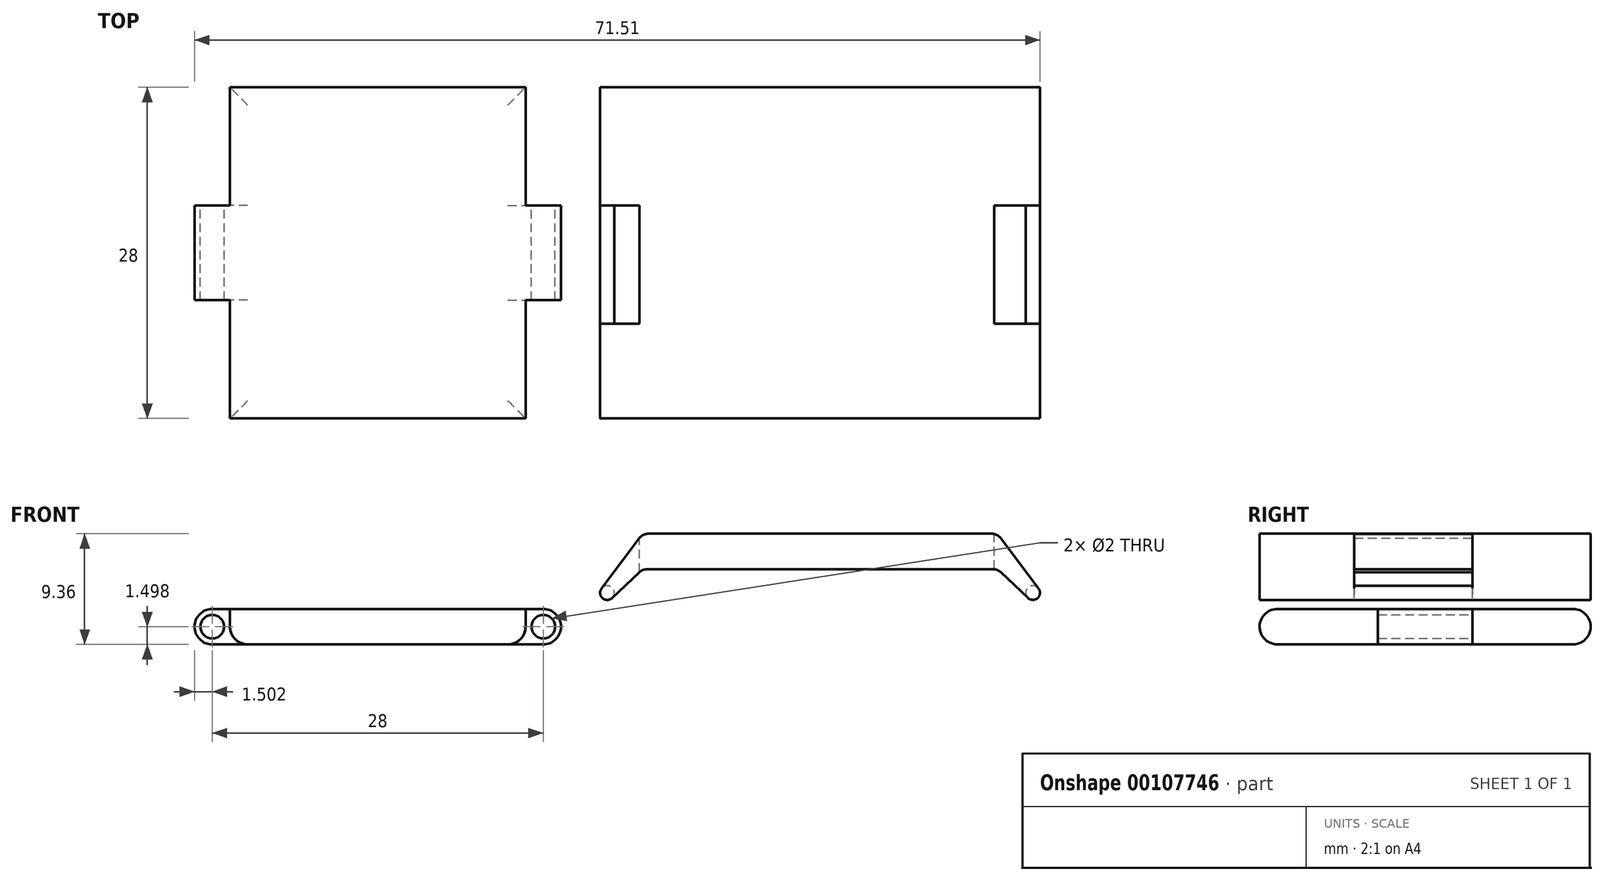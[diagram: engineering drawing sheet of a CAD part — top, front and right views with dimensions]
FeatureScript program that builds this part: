
annotation { "Feature Type Name" : "Feature", "Feature Type Description" : "" }
export const myFeature = defineFeature(function(context is Context, id is Id, definition is map)
    precondition{}
    {
        {
            var Q0;
            Q0=qCreatedBy(makeId("Front.planeOp"),FACE);
            var sketch = newSketch(context, id + "F0", { "sketchPlane" : qUnion([Q0])});
            skLineSegment(sketch, "E0.bottom", {"start": v(-39.04, 3) * mm, "end": v(-11.04, 3) * mm});
            skLineSegment(sketch, "E0.top", {"start": v(-39.04, 0) * mm, "end": v(-11.04, 0) * mm});
            skLineSegment(sketch, "E0.left", {"start": v(-39.04, 3) * mm, "end": v(-39.04, 2.5) * mm});
            skLineSegment(sketch, "E0.right", {"start": v(-11.04, 3) * mm, "end": v(-11.04, 2.5) * mm});
            skArc(sketch, "E1", {"start": v(-11.04, 0) * mm, "mid": v(-9.54, 1.5) * mm, "end": v(-11.04, 3) * mm});
            skArc(sketch, "E2", {"start": v(-39.04, 3) * mm, "mid": v(-40.54, 1.5) * mm, "end": v(-39.04, 0) * mm});
            skCircle(sketch, "E3", {"center": v(-39.04, 1.5) * mm, "radius": 1 * mm});
            skCircle(sketch, "E4", {"center": v(-11.04, 1.5) * mm, "radius": 1 * mm});
            skLineSegment(sketch, "E5.trimOffspring", {"start": v(-11.04, 0.5) * mm, "end": v(-11.04, 0) * mm});
            skLineSegment(sketch, "E6.trimOffspring", {"start": v(-39.04, 0.5) * mm, "end": v(-39.04, 0) * mm});
            skLineSegment(sketch, "E7.bottom", {"start": v(-2.27, 6.37) * mm, "end": v(26.94, 6.37) * mm});
            skLineSegment(sketch, "E7.top", {"start": v(-2.16, 9.37) * mm, "end": v(26.84, 9.37) * mm});
            skLineSegment(sketch, "E7.left", {"start": v(-2.66, 6.37) * mm, "end": v(-2.66, 9.37) * mm});
            skLineSegment(sketch, "E7.right", {"start": v(27.34, 6.37) * mm, "end": v(27.34, 9.37) * mm});
            skCircle(sketch, "E8", {"center": v(30.34, 4.37) * mm, "radius": 0.6 * mm});
            skCircle(sketch, "E9", {"center": v(-5.66, 4.37) * mm, "radius": 0.6 * mm});
            skLineSegment(sketch, "E10", {"start": v(-2.96, 8.97) * mm, "end": v(-6.14, 4.73) * mm});
            skLineSegment(sketch, "E11", {"start": v(-2.95, 6.1) * mm, "end": v(-5.25, 3.93) * mm});
            skLineSegment(sketch, "E12", {"start": v(27.64, 8.97) * mm, "end": v(30.82, 4.73) * mm});
            skLineSegment(sketch, "E13", {"start": v(27.62, 6.1) * mm, "end": v(29.92, 3.94) * mm});
            skPoint(sketch, "E14.visualSharp", {"position": v(-2.66, 9.37) * mm});
            skArc(sketch, "E14.filletArc", {"start": v(-2.16, 9.37) * mm, "mid": v(-2.61, 9.27) * mm, "end": v(-2.96, 8.97) * mm});
            skPoint(sketch, "E15.visualSharp", {"position": v(-2.66, 6.37) * mm});
            skArc(sketch, "E15.filletArc", {"start": v(-2.27, 6.37) * mm, "mid": v(-2.64, 6.3) * mm, "end": v(-2.95, 6.1) * mm});
            skPoint(sketch, "E16.visualSharp", {"position": v(27.34, 9.37) * mm});
            skArc(sketch, "E16.filletArc", {"start": v(27.64, 8.97) * mm, "mid": v(27.28, 9.27) * mm, "end": v(26.84, 9.37) * mm});
            skPoint(sketch, "E17.visualSharp", {"position": v(27.34, 6.37) * mm});
            skArc(sketch, "E17.filletArc", {"start": v(27.62, 6.1) * mm, "mid": v(27.3, 6.3) * mm, "end": v(26.94, 6.37) * mm});
            skSolve(sketch);
        }
        {
            var Q0;
            Q0=makeQuery(id+"F0.imprint","IMPRINT",FACE,{"disambiguationData":[TD([[makeQuery(id+"F0.imprint","IMPRINT",EDGE,{"derivedFrom":sQuery(id+"F0.wireOp",EDGE,"E0.bottom")}),-1.0]])]});
            var sketch = newSketch(context, id + "F1", { "sketchPlane" : qUnion([Q0])});
            skLineSegment(sketch, "E18.bottom", {"start": v(-39.07, 3) * mm, "end": v(-11.07, 3) * mm});
            skLineSegment(sketch, "E18.top", {"start": v(-39.07, 0) * mm, "end": v(-11.07, 0) * mm});
            skLineSegment(sketch, "E18.left", {"start": v(-39.07, 3) * mm, "end": v(-39.07, 2.5) * mm});
            skLineSegment(sketch, "E18.right", {"start": v(-11.07, 3) * mm, "end": v(-11.07, 2.5) * mm});
            skArc(sketch, "E19", {"start": v(-11.07, 0) * mm, "mid": v(-9.57, 1.5) * mm, "end": v(-11.07, 3) * mm});
            skArc(sketch, "E20", {"start": v(-39.07, 3) * mm, "mid": v(-40.57, 1.5) * mm, "end": v(-39.07, 0) * mm});
            skCircle(sketch, "E21", {"center": v(-39.07, 1.5) * mm, "radius": 1 * mm});
            skCircle(sketch, "E22", {"center": v(-11.07, 1.5) * mm, "radius": 1 * mm});
            skLineSegment(sketch, "E23.trimOffspring", {"start": v(-11.07, 0.5) * mm, "end": v(-11.07, 0) * mm});
            skLineSegment(sketch, "E24.trimOffspring", {"start": v(-39.07, 0.5) * mm, "end": v(-39.07, 0) * mm});
            skSolve(sketch);
        }
        {
            var Q0;
            Q0 = qSketchRegion(id + "F1", true);
            extrude(context, id + "F2", {"entities" : qUnion([Q0]), "depth" : 28 * mm});
        }
        {
            var Q0;
            Q0=makeQuery(id+"F0.imprint","IMPRINT",FACE,{"disambiguationData":[TD([[makeQuery(id+"F0.imprint","IMPRINT",EDGE,{"derivedFrom":sQuery(id+"F0.wireOp",EDGE,"E7.right")}),-1.0]])]});
            var Q1;
            Q1=makeQuery(id+"F0.imprint","IMPRINT",FACE,{"disambiguationData":[TD([[makeQuery(id+"F0.imprint","IMPRINT",EDGE,{"derivedFrom":sQuery(id+"F0.wireOp",EDGE,"E7.left")}),1.0]])]});
            var Q2;
            Q2=makeQuery(id+"F0.imprint","IMPRINT",FACE,{"disambiguationData":[TD([[makeQuery(id+"F0.imprint","IMPRINT",EDGE,{"derivedFrom":sQuery(id+"F0.wireOp",EDGE,"E7.bottom")}),1.0]])]});
            var Q3;
            {var subQ0=sQuery(id+"F0.wireOp",EDGE,"E9");var subQ1=makeQuery(id+"F0.imprint","INTERSECT",VERTEX,{"derivedFrom":[subQ0,sQuery(id+"F0.wireOp",EDGE,"E10")]});Q3=makeQuery(id+"F0.imprint","IMPRINT",FACE,{"disambiguationData":[TD([[makeQuery(id+"F0.imprint","IMPRINT",EDGE,{"disambiguationData":[TD([[subQ1,-1.0]])],"derivedFrom":subQ0}),1.0]])]});}
            var Q4;
            {var subQ0=sQuery(id+"F0.wireOp",EDGE,"E8");var subQ1=makeQuery(id+"F0.imprint","INTERSECT",VERTEX,{"derivedFrom":[subQ0,sQuery(id+"F0.wireOp",EDGE,"E12")]});Q4=makeQuery(id+"F0.imprint","IMPRINT",FACE,{"disambiguationData":[TD([[makeQuery(id+"F0.imprint","IMPRINT",EDGE,{"disambiguationData":[TD([[subQ1,-1.0]])],"derivedFrom":subQ0}),1.0]])]});}
            extrude(context, id + "F3", {"entities" : qUnion([Q0, Q1, Q2, Q3, Q4]), "depth" : 28 * mm});
        }
        {
            var Q0;
            Q0=makeQuery(id+"F3.opExtrude","SWEPT_FACE",FACE,{"disambiguationData":[OSD([sQuery(id+"F0.wireOp",EDGE,"E7.top")])]});
            var sketch = newSketch(context, id + "F4", { "sketchPlane" : qUnion([Q0])});
            skLineSegment(sketch, "E25", {"start": v(27.07, -15) * mm, "end": v(27.07, -10) * mm});
            skLineSegment(sketch, "E26", {"start": v(27.07, -10) * mm, "end": v(31.07, -10) * mm});
            skLineSegment(sketch, "E27", {"start": v(31.07, -10) * mm, "end": v(31.07, -20) * mm});
            skLineSegment(sketch, "E28", {"start": v(31.07, -20) * mm, "end": v(27.07, -20) * mm});
            skLineSegment(sketch, "E29", {"start": v(27.07, -20) * mm, "end": v(27.07, -15) * mm});
            skLineSegment(sketch, "E30", {"start": v(-2.93, -15) * mm, "end": v(-2.93, -10) * mm});
            skLineSegment(sketch, "E31", {"start": v(-2.93, -10) * mm, "end": v(-6.93, -10) * mm});
            skLineSegment(sketch, "E32", {"start": v(-6.93, -10) * mm, "end": v(-6.93, -20) * mm});
            skLineSegment(sketch, "E33", {"start": v(-6.93, -20) * mm, "end": v(-2.93, -20) * mm});
            skLineSegment(sketch, "E34", {"start": v(-2.93, -20) * mm, "end": v(-2.93, -15) * mm});
            skSolve(sketch);
        }
        {
            var Q0;
            Q0 = qSketchRegion(id + "F4", true);
            extrude(context, id + "F5", {"entities" : qUnion([Q0]), "operationType" : NewBodyOperationType.REMOVE, "oppositeDirection" : true, "depth" : 25 * mm});
        }
        {
            var Q0;
            Q0=makeQuery(id+"F5.boolean.opBoolean","COPY",FACE,{"derivedFrom":makeQuery(id+"F5.opExtrude","SWEPT_FACE",FACE,{"disambiguationData":[OSD([sQuery(id+"F4.wireOp",EDGE,"E26")])]})});
            var sketch = newSketch(context, id + "F6", { "sketchPlane" : qUnion([Q0])});
            skCircle(sketch, "E35", {"center": v(30.34, 4.37) * mm, "radius": 0.6 * mm});
            skSolve(sketch);
        }
        {
            var Q0;
            Q0 = qSketchRegion(id + "F6", true);
            extrude(context, id + "F7", {"entities" : qUnion([Q0]), "operationType" : NewBodyOperationType.ADD, "depth" : 12 * mm});
        }
        {
            var Q0;
            Q0=makeQuery(id+"F5.boolean.opBoolean","COPY",FACE,{"derivedFrom":makeQuery(id+"F5.opExtrude","SWEPT_FACE",FACE,{"disambiguationData":[OSD([sQuery(id+"F4.wireOp",EDGE,"E31")])]})});
            var sketch = newSketch(context, id + "F8", { "sketchPlane" : qUnion([Q0])});
            skCircle(sketch, "E36", {"center": v(-5.66, 4.37) * mm, "radius": 0.6 * mm});
            skSolve(sketch);
        }
        {
            var Q0;
            Q0 = qSketchRegion(id + "F8", true);
            extrude(context, id + "F9", {"entities" : qUnion([Q0]), "operationType" : NewBodyOperationType.ADD, "depth" : 12 * mm});
        }
        {
            var Q0;
            Q0=makeQuery(id+"F2.opExtrude","SWEPT_FACE",FACE,{"disambiguationData":[OSD([sQuery(id+"F1.wireOp",EDGE,"E18.bottom")])]});
            var sketch = newSketch(context, id + "F10", { "sketchPlane" : qUnion([Q0])});
            skLineSegment(sketch, "E37", {"start": v(-39.07, 0) * mm, "end": v(-37.57, 0) * mm});
            skLineSegment(sketch, "E38", {"start": v(-37.57, 0) * mm, "end": v(-37.57, -10) * mm});
            skLineSegment(sketch, "E39", {"start": v(-37.57, -10) * mm, "end": v(-41.57, -10) * mm});
            skLineSegment(sketch, "E40", {"start": v(-41.57, -10) * mm, "end": v(-41.57, 0) * mm});
            skLineSegment(sketch, "E41", {"start": v(-41.57, 0) * mm, "end": v(-39.07, 0) * mm});
            skLineSegment(sketch, "E42", {"start": v(-39.07, -28) * mm, "end": v(-37.57, -28) * mm});
            skLineSegment(sketch, "E43", {"start": v(-37.57, -28) * mm, "end": v(-37.57, -18) * mm});
            skLineSegment(sketch, "E44", {"start": v(-37.57, -18) * mm, "end": v(-41.57, -18) * mm});
            skLineSegment(sketch, "E45", {"start": v(-41.57, -18) * mm, "end": v(-41.57, -28) * mm});
            skLineSegment(sketch, "E46", {"start": v(-41.57, -28) * mm, "end": v(-39.07, -28) * mm});
            skLineSegment(sketch, "E47", {"start": v(-11.07, 0) * mm, "end": v(-12.57, 0) * mm});
            skLineSegment(sketch, "E48", {"start": v(-12.57, 0) * mm, "end": v(-12.57, -10) * mm});
            skLineSegment(sketch, "E49", {"start": v(-12.57, -10) * mm, "end": v(-8.57, -10) * mm});
            skLineSegment(sketch, "E50", {"start": v(-8.57, -10) * mm, "end": v(-8.57, 0) * mm});
            skLineSegment(sketch, "E51", {"start": v(-8.57, 0) * mm, "end": v(-11.07, 0) * mm});
            skLineSegment(sketch, "E52", {"start": v(-11.07, -28) * mm, "end": v(-12.57, -28) * mm});
            skLineSegment(sketch, "E53", {"start": v(-12.57, -28) * mm, "end": v(-12.57, -18) * mm});
            skLineSegment(sketch, "E54", {"start": v(-12.57, -18) * mm, "end": v(-8.57, -18) * mm});
            skLineSegment(sketch, "E55", {"start": v(-8.57, -18) * mm, "end": v(-8.57, -28) * mm});
            skLineSegment(sketch, "E56", {"start": v(-8.57, -28) * mm, "end": v(-11.07, -28) * mm});
            skSolve(sketch);
        }
        {
            var Q0;
            Q0 = qSketchRegion(id + "F10", true);
            extrude(context, id + "F11", {"entities" : qUnion([Q0]), "operationType" : NewBodyOperationType.REMOVE, "oppositeDirection" : true, "depth" : 25 * mm});
        }
        {
            var Q0;
            Q0=makeQuery(id+"F2.opExtrude","CAP_EDGE",EDGE,{"disambiguationData":[OSD([sQuery(id+"F1.wireOp",EDGE,"E18.bottom")])],"isStart":false});
            var Q1;
            Q1=makeQuery(id+"F2.opExtrude","CAP_EDGE",EDGE,{"disambiguationData":[OSD([sQuery(id+"F1.wireOp",EDGE,"E18.bottom")])],"isStart":true});
            var Q2;
            Q2=makeQuery(id+"F11.boolean.opBoolean","COPY",EDGE,{"derivedFrom":makeQuery(id+"F11.opExtrude","CAP_EDGE",EDGE,{"disambiguationData":[OSD([sQuery(id+"F10.wireOp",EDGE,"E48")])],"isStart":true})});
            var Q3;
            Q3=makeQuery(id+"F11.boolean.opBoolean","COPY",EDGE,{"derivedFrom":makeQuery(id+"F11.opExtrude","CAP_EDGE",EDGE,{"disambiguationData":[OSD([sQuery(id+"F10.wireOp",EDGE,"E53")])],"isStart":true})});
            var Q4;
            Q4=makeQuery(id+"F11.boolean.opBoolean","COPY",EDGE,{"derivedFrom":makeQuery(id+"F11.opExtrude","CAP_EDGE",EDGE,{"disambiguationData":[OSD([sQuery(id+"F10.wireOp",EDGE,"E43")])],"isStart":true})});
            var Q5;
            Q5=makeQuery(id+"F11.boolean.opBoolean","COPY",EDGE,{"derivedFrom":makeQuery(id+"F11.opExtrude","CAP_EDGE",EDGE,{"disambiguationData":[OSD([sQuery(id+"F10.wireOp",EDGE,"E38")])],"isStart":true})});
            var Q6;
            Q6=makeQuery(id+"F2.opExtrude","CAP_EDGE",EDGE,{"disambiguationData":[OSD([sQuery(id+"F1.wireOp",EDGE,"E18.top")])],"isStart":true});
            var Q7;
            Q7=makeQuery(id+"F11.boolean.opBoolean","INTERSECT",EDGE,{"derivedFrom":[makeQuery(id+"F2.opExtrude","SWEPT_FACE",FACE,{"disambiguationData":[OSD([sQuery(id+"F1.wireOp",EDGE,"E18.top")])]}),makeQuery(id+"F11.opExtrude","SWEPT_FACE",FACE,{"disambiguationData":[OSD([sQuery(id+"F10.wireOp",EDGE,"E38")])]})]});
            var Q8;
            Q8=makeQuery(id+"F11.boolean.opBoolean","INTERSECT",EDGE,{"derivedFrom":[makeQuery(id+"F2.opExtrude","SWEPT_FACE",FACE,{"disambiguationData":[OSD([sQuery(id+"F1.wireOp",EDGE,"E18.top")])]}),makeQuery(id+"F11.opExtrude","SWEPT_FACE",FACE,{"disambiguationData":[OSD([sQuery(id+"F10.wireOp",EDGE,"E43")])]})]});
            var Q9;
            Q9=makeQuery(id+"F2.opExtrude","CAP_EDGE",EDGE,{"disambiguationData":[OSD([sQuery(id+"F1.wireOp",EDGE,"E18.top")])],"isStart":false});
            var Q10;
            Q10=makeQuery(id+"F11.boolean.opBoolean","INTERSECT",EDGE,{"derivedFrom":[makeQuery(id+"F2.opExtrude","SWEPT_FACE",FACE,{"disambiguationData":[OSD([sQuery(id+"F1.wireOp",EDGE,"E18.top")])]}),makeQuery(id+"F11.opExtrude","SWEPT_FACE",FACE,{"disambiguationData":[OSD([sQuery(id+"F10.wireOp",EDGE,"E53")])]})]});
            var Q11;
            Q11=makeQuery(id+"F11.boolean.opBoolean","INTERSECT",EDGE,{"derivedFrom":[makeQuery(id+"F2.opExtrude","SWEPT_FACE",FACE,{"disambiguationData":[OSD([sQuery(id+"F1.wireOp",EDGE,"E18.top")])]}),makeQuery(id+"F11.opExtrude","SWEPT_FACE",FACE,{"disambiguationData":[OSD([sQuery(id+"F10.wireOp",EDGE,"E48")])]})]});
            fillet(context, id + "F12", {"entities" : qUnion([Q0, Q1, Q2, Q3, Q4, Q5, Q6, Q7, Q8, Q9, Q10, Q11]), "radius" : 1.5 * mm, "tangentPropagation" : true, "allowEdgeOverflow" : false});
        }
    });
